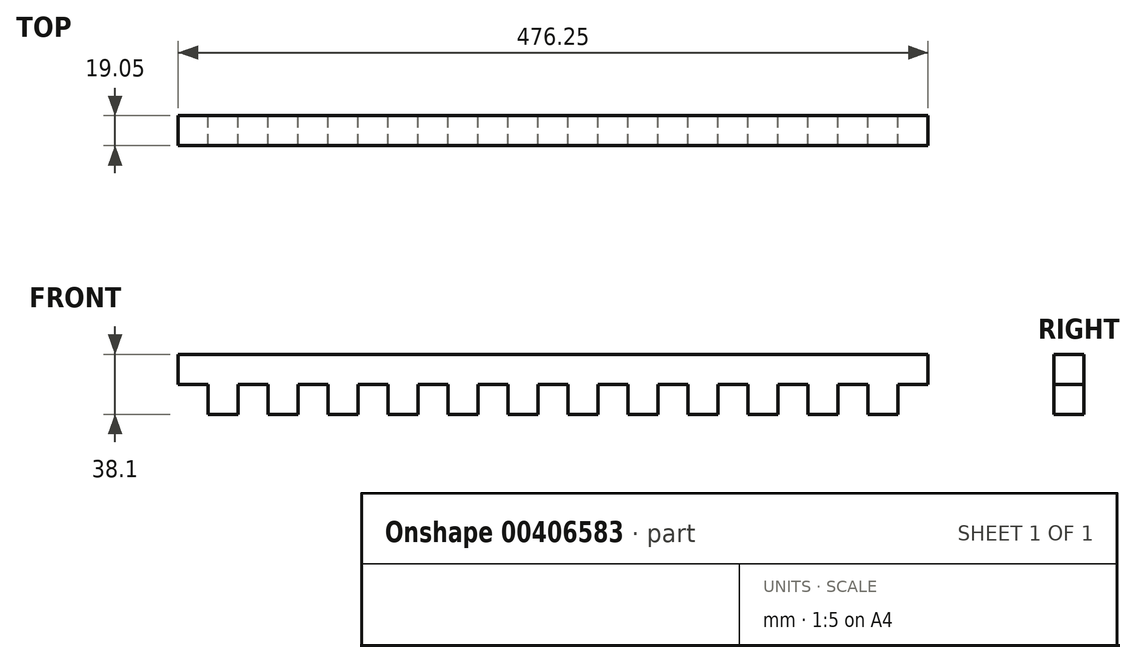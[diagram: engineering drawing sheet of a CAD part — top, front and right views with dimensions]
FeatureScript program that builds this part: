
annotation { "Feature Type Name" : "Feature", "Feature Type Description" : "" }
export const myFeature = defineFeature(function(context is Context, id is Id, definition is map)
    precondition{}
    {
        {
            var Q0;
            Q0=qCreatedBy(makeId("Front.planeOp"),FACE);
            var sketch = newSketch(context, id + "F0", { "sketchPlane" : qUnion([Q0])});
            skLineSegment(sketch, "E0", {"start": v(0, 0) * mm, "end": v(476.25, 0) * mm});
            skLineSegment(sketch, "E1", {"start": v(67.44, -38.1) * mm, "end": v(57.15, -38.1) * mm});
            skLineSegment(sketch, "E2", {"start": v(57.15, -19.05) * mm, "end": v(48.39, -19.05) * mm});
            skLineSegment(sketch, "E3", {"start": v(19.05, -38.1) * mm, "end": v(19.05, -19.05) * mm});
            skLineSegment(sketch, "E4", {"start": v(19.05, -19.05) * mm, "end": v(0, -19.05) * mm});
            skLineSegment(sketch, "E5", {"start": v(0, -19.05) * mm, "end": v(0, 0) * mm});
            skLineSegment(sketch, "E6", {"start": v(38.1, -19.05) * mm, "end": v(57.15, -19.05) * mm});
            skLineSegment(sketch, "E7", {"start": v(57.15, -19.05) * mm, "end": v(57.15, -38.1) * mm});
            skLineSegment(sketch, "E8", {"start": v(57.15, -38.1) * mm, "end": v(76.2, -38.1) * mm});
            skLineSegment(sketch, "E9", {"start": v(76.2, -38.1) * mm, "end": v(76.2, -19.05) * mm});
            skLineSegment(sketch, "E10", {"start": v(76.2, -19.05) * mm, "end": v(95.25, -19.05) * mm});
            skLineSegment(sketch, "E11", {"start": v(95.25, -19.05) * mm, "end": v(95.25, -38.1) * mm});
            skLineSegment(sketch, "E12", {"start": v(95.25, -38.1) * mm, "end": v(114.3, -38.1) * mm});
            skLineSegment(sketch, "E13", {"start": v(114.3, -38.1) * mm, "end": v(114.3, -19.05) * mm});
            skLineSegment(sketch, "E14", {"start": v(114.3, -19.05) * mm, "end": v(133.35, -19.05) * mm});
            skLineSegment(sketch, "E15", {"start": v(133.35, -19.05) * mm, "end": v(133.35, -38.1) * mm});
            skLineSegment(sketch, "E16", {"start": v(133.35, -38.1) * mm, "end": v(152.4, -38.1) * mm});
            skLineSegment(sketch, "E17", {"start": v(152.4, -38.1) * mm, "end": v(152.4, -19.05) * mm});
            skLineSegment(sketch, "E18", {"start": v(152.4, -19.05) * mm, "end": v(171.45, -19.05) * mm});
            skLineSegment(sketch, "E19", {"start": v(171.45, -19.05) * mm, "end": v(171.45, -38.1) * mm});
            skLineSegment(sketch, "E20", {"start": v(171.45, -38.1) * mm, "end": v(190.5, -38.1) * mm});
            skLineSegment(sketch, "E21", {"start": v(190.5, -38.1) * mm, "end": v(190.5, -19.05) * mm});
            skLineSegment(sketch, "E22", {"start": v(190.5, -19.05) * mm, "end": v(209.55, -19.05) * mm});
            skLineSegment(sketch, "E23", {"start": v(209.55, -19.05) * mm, "end": v(209.55, -38.1) * mm});
            skLineSegment(sketch, "E24", {"start": v(209.55, -38.1) * mm, "end": v(228.6, -38.1) * mm});
            skLineSegment(sketch, "E25", {"start": v(228.6, -38.1) * mm, "end": v(228.6, -19.05) * mm});
            skLineSegment(sketch, "E26", {"start": v(228.6, -19.05) * mm, "end": v(247.65, -19.05) * mm});
            skLineSegment(sketch, "E27", {"start": v(247.65, -19.05) * mm, "end": v(247.65, -38.1) * mm});
            skLineSegment(sketch, "E28", {"start": v(247.65, -38.1) * mm, "end": v(266.7, -38.1) * mm});
            skLineSegment(sketch, "E29", {"start": v(266.7, -38.1) * mm, "end": v(266.7, -19.05) * mm});
            skLineSegment(sketch, "E30", {"start": v(266.7, -19.05) * mm, "end": v(285.75, -19.05) * mm});
            skLineSegment(sketch, "E31", {"start": v(285.75, -19.05) * mm, "end": v(285.75, -38.1) * mm});
            skLineSegment(sketch, "E32", {"start": v(285.75, -38.1) * mm, "end": v(304.8, -38.1) * mm});
            skLineSegment(sketch, "E33", {"start": v(304.8, -38.1) * mm, "end": v(304.8, -19.05) * mm});
            skLineSegment(sketch, "E34", {"start": v(304.8, -19.05) * mm, "end": v(323.85, -19.05) * mm});
            skLineSegment(sketch, "E35", {"start": v(323.85, -19.05) * mm, "end": v(323.85, -38.1) * mm});
            skLineSegment(sketch, "E36", {"start": v(323.85, -38.1) * mm, "end": v(342.9, -38.1) * mm});
            skLineSegment(sketch, "E37", {"start": v(342.9, -38.1) * mm, "end": v(342.9, -19.05) * mm});
            skLineSegment(sketch, "E38", {"start": v(342.9, -19.05) * mm, "end": v(361.95, -19.05) * mm});
            skLineSegment(sketch, "E39", {"start": v(361.95, -19.05) * mm, "end": v(361.95, -38.1) * mm});
            skLineSegment(sketch, "E40", {"start": v(361.95, -38.1) * mm, "end": v(381, -38.1) * mm});
            skLineSegment(sketch, "E41", {"start": v(381, -38.1) * mm, "end": v(381, -19.05) * mm});
            skLineSegment(sketch, "E42", {"start": v(381, -19.05) * mm, "end": v(400.05, -19.05) * mm});
            skLineSegment(sketch, "E43", {"start": v(400.05, -19.05) * mm, "end": v(400.05, -38.1) * mm});
            skLineSegment(sketch, "E44", {"start": v(400.05, -38.1) * mm, "end": v(419.1, -38.1) * mm});
            skLineSegment(sketch, "E45", {"start": v(419.1, -38.1) * mm, "end": v(419.1, -19.05) * mm});
            skLineSegment(sketch, "E46", {"start": v(419.1, -19.05) * mm, "end": v(438.15, -19.05) * mm});
            skLineSegment(sketch, "E47", {"start": v(438.15, -19.05) * mm, "end": v(438.15, -38.1) * mm});
            skLineSegment(sketch, "E48", {"start": v(438.15, -38.1) * mm, "end": v(457.2, -38.1) * mm});
            skLineSegment(sketch, "E49", {"start": v(457.2, -38.1) * mm, "end": v(457.2, -19.05) * mm});
            skLineSegment(sketch, "E50", {"start": v(457.2, -19.05) * mm, "end": v(476.25, -19.05) * mm});
            skLineSegment(sketch, "E51", {"start": v(476.25, -19.05) * mm, "end": v(476.25, 0) * mm});
            skPoint(sketch, "E52.end.orphan", {"position": v(542.16, 0) * mm});
            skPoint(sketch, "E53.end.orphan", {"position": v(533.4, -19.05) * mm});
            skPoint(sketch, "E54.end.orphan", {"position": v(514.35, -38.1) * mm});
            skPoint(sketch, "E55.end.orphan", {"position": v(495.3, -19.05) * mm});
            skPoint(sketch, "E56.start.orphan", {"position": v(476.25, -38.1) * mm});
            skPoint(sketch, "E57.end.orphan", {"position": v(1026.29, -19.05) * mm});
            skPoint(sketch, "E58.end.orphan", {"position": v(67.44, -19.05) * mm});
            skPoint(sketch, "E59.orphan", {"position": v(48.39, -38.1) * mm});
            skLineSegment(sketch, "E60", {"start": v(19.05, -38.1) * mm, "end": v(38.1, -38.1) * mm});
            skLineSegment(sketch, "E61", {"start": v(38.1, -38.1) * mm, "end": v(38.1, -19.05) * mm});
            skSolve(sketch);
        }
        {
            var Q0;
            Q0=makeQuery(id+"F0.imprint","IMPRINT",FACE,{"disambiguationData":[TD([[makeQuery(id+"F0.imprint","IMPRINT",EDGE,{"derivedFrom":sQuery(id+"F0.wireOp",EDGE,"E0")}),-1.0]])]});
            extrude(context, id + "F1", {"entities" : qUnion([Q0]), "depth" : 19.05 * mm});
        }
    });
